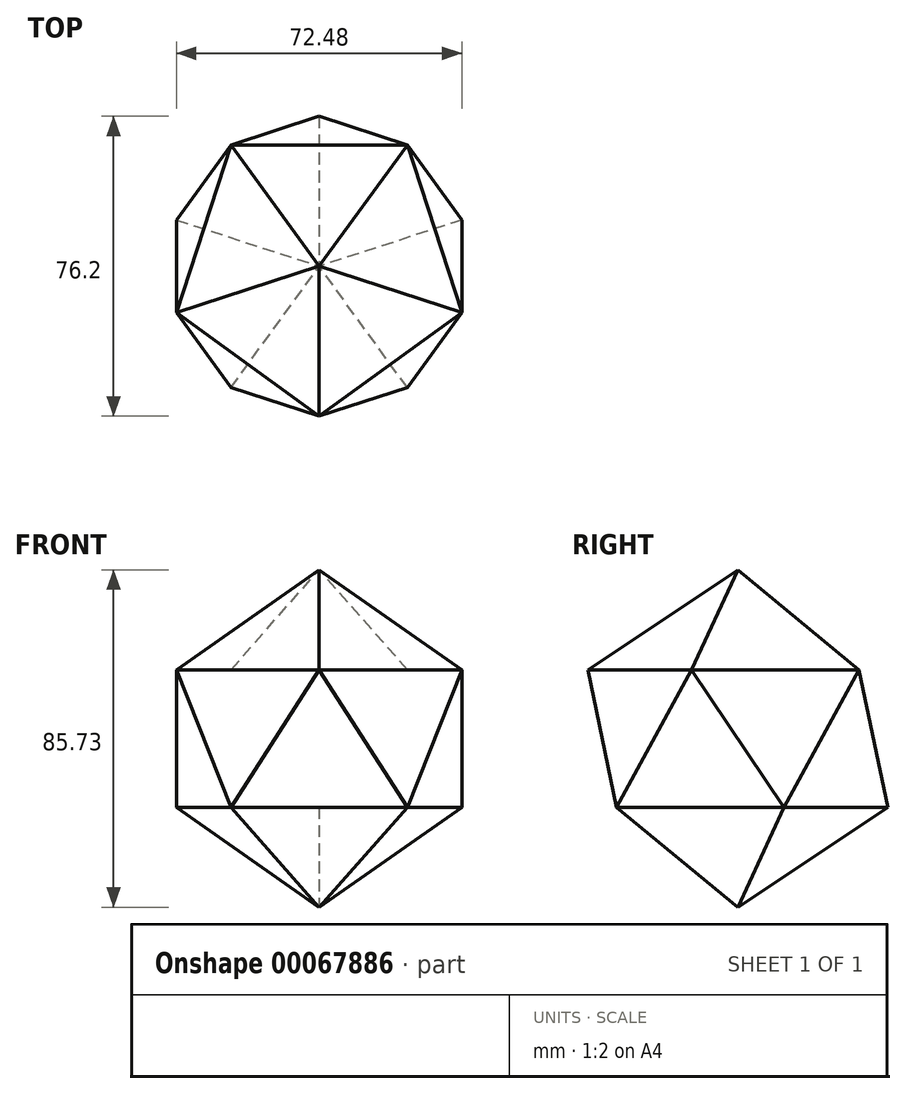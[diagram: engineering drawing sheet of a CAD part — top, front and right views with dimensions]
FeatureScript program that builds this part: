
annotation { "Feature Type Name" : "Feature", "Feature Type Description" : "" }
export const myFeature = defineFeature(function(context is Context, id is Id, definition is map)
    precondition{}
    {
        {
            var Q0;
            Q0=qCreatedBy(makeId("Top.planeOp"),FACE);
            var sketch = newSketch(context, id + "F0", { "sketchPlane" : qUnion([Q0])});
            skPoint(sketch, "E0", {"position": v(0, 0) * mm});
            skSolve(sketch);
        }
        {
            var Q0;
            Q0=qCreatedBy(makeId("Top.planeOp"),FACE);
            cPlane(context, id + "F1", {"entities" : qUnion([Q0]), "cplaneType" : CPlaneType.OFFSET, "offset" : 25.4 * mm, "width" : 152.4 * mm, "height" : 152.4 * mm});
        }
        {
            var Q0;
            Q0=qCreatedBy(id+"F1.planeOp",FACE);
            cPlane(context, id + "F2", {"entities" : qUnion([Q0]), "cplaneType" : CPlaneType.OFFSET, "offset" : 34.92 * mm, "width" : 152.4 * mm, "height" : 152.4 * mm});
        }
        {
            var Q0;
            Q0=qCreatedBy(id+"F2.planeOp",FACE);
            cPlane(context, id + "F3", {"entities" : qUnion([Q0]), "cplaneType" : CPlaneType.OFFSET, "offset" : 25.4 * mm, "width" : 152.4 * mm, "height" : 152.4 * mm});
        }
        {
            var Q0;
            Q0=qCreatedBy(id+"F1.planeOp",FACE);
            var sketch = newSketch(context, id + "F4", { "sketchPlane" : qUnion([Q0])});
            skCircle(sketch, "E1.cCircle", {"center": v(0, 0) * mm, "radius": 38.1 * mm, "construction": true});
            skLineSegment(sketch, "E1.0", {"start": v(-36.24, 11.77) * mm, "end": v(0, 38.1) * mm});
            skLineSegment(sketch, "E1.1", {"start": v(0, 38.1) * mm, "end": v(36.24, 11.77) * mm});
            skLineSegment(sketch, "E1.2", {"start": v(36.24, 11.77) * mm, "end": v(22.4, -30.82) * mm});
            skLineSegment(sketch, "E1.3", {"start": v(22.4, -30.82) * mm, "end": v(-22.4, -30.82) * mm});
            skLineSegment(sketch, "E1.4", {"start": v(-22.4, -30.82) * mm, "end": v(-36.24, 11.77) * mm});
            skSolve(sketch);
        }
        {
            var Q0;
            Q0=qCreatedBy(id+"F2.planeOp",FACE);
            var sketch = newSketch(context, id + "F5", { "sketchPlane" : qUnion([Q0])});
            skCircle(sketch, "E2.cCircle", {"center": v(0, 0) * mm, "radius": 38.1 * mm, "construction": true});
            skLineSegment(sketch, "E2.0", {"start": v(0, -38.1) * mm, "end": v(-36.24, -11.77) * mm});
            skLineSegment(sketch, "E2.1", {"start": v(-36.24, -11.77) * mm, "end": v(-22.4, 30.82) * mm});
            skLineSegment(sketch, "E2.2", {"start": v(-22.4, 30.82) * mm, "end": v(22.4, 30.82) * mm});
            skLineSegment(sketch, "E2.3", {"start": v(22.4, 30.82) * mm, "end": v(36.24, -11.77) * mm});
            skLineSegment(sketch, "E2.4", {"start": v(36.24, -11.77) * mm, "end": v(0, -38.1) * mm});
            skSolve(sketch);
        }
        {
            var Q0;
            Q0=qCreatedBy(id+"F3.planeOp",FACE);
            var sketch = newSketch(context, id + "F6", { "sketchPlane" : qUnion([Q0])});
            skPoint(sketch, "E3", {"position": v(0, 0) * mm});
            skSolve(sketch);
        }
        {
            var Q0;
            Q0=sQuery(id+"F4.wireOp",EDGE,"E1.3");
            var Q1;
            Q1=sQuery(id+"F5.wireOp",VERTEX,"E2.4.end");
            loft(context, id + "F7", {"bodyType" : ToolBodyType.SURFACE, "wireProfilesArray" : [{ "wireProfileEntities" : qUnion([Q0]) }, { "wireProfileEntities" : qUnion([Q1]) }]});
        }
        {
            var Q0;
            Q0=qCreatedBy(makeId("Right.planeOp"),FACE);
            var sketch = newSketch(context, id + "F8", { "sketchPlane" : qUnion([Q0])});
            skLineSegment(sketch, "E4", {"start": v(0, -22.28) * mm, "end": v(0, 85.26) * mm, "construction": true});
            skSolve(sketch);
        }
        {
            var Q0;
            Q0=makeQuery(id+"F7.opLoft","SWEPT_BODY",BODY,{"disambiguationData":[OSD([sQuery(id+"F4.wireOp",EDGE,"E1.3"),sQuery(id+"F5.wireOp",VERTEX,"E2.4.end")])]});
            var Q1;
            Q1=sQuery(id+"F8.wireOp",EDGE,"E4");
            circularPattern(context, id + "F9", {"entities" : qUnion([Q0]), "axis" : qUnion([Q1]), "angle" : 360 * degree, "instanceCount" : 5, "equalSpace" : true});
        }
        {
            var Q0;
            Q0=sQuery(id+"F4.wireOp",VERTEX,"E1.3.start");
            var Q1;
            Q1=makeQuery(id+"F5.imprint","IMPRINT",FACE,{"disambiguationData":[TD([[makeQuery(id+"F5.imprint","IMPRINT",EDGE,{"derivedFrom":sQuery(id+"F5.wireOp",EDGE,"E2.0")}),-1.0]])]});
            var Q2;
            Q2=sQuery(id+"F4.wireOp",VERTEX,"E1.4.start");
            var Q3;
            Q3=sQuery(id+"F5.wireOp",EDGE,"E2.0");
            loft(context, id + "F10", {"bodyType" : ToolBodyType.SURFACE, "sheetProfilesArray" : [{ "sheetProfileEntities" : qUnion([Q0]) }, { "sheetProfileEntities" : qUnion([Q1]) }], "wireProfilesArray" : [{ "wireProfileEntities" : qUnion([Q2]) }, { "wireProfileEntities" : qUnion([Q3]) }]});
        }
        {
            var Q0;
            Q0=qCreatedBy(makeId("Right.planeOp"),FACE);
            var sketch = newSketch(context, id + "F11", { "sketchPlane" : qUnion([Q0])});
            skLineSegment(sketch, "E5", {"start": v(0, -11.8) * mm, "end": v(0, 95.91) * mm, "construction": true});
            skSolve(sketch);
        }
        {
            var Q0;
            Q0=makeQuery(id+"F10.opLoft","SWEPT_BODY",BODY,{"disambiguationData":[OSD([sQuery(id+"F4.wireOp",VERTEX,"E1.4.start"),sQuery(id+"F5.wireOp",EDGE,"E2.0")])]});
            var Q1;
            Q1=sQuery(id+"F11.wireOp",EDGE,"E5");
            circularPattern(context, id + "F12", {"entities" : qUnion([Q0]), "axis" : qUnion([Q1]), "angle" : 360 * degree, "instanceCount" : 5, "equalSpace" : true});
        }
        {
            var Q0;
            Q0 = qSketchRegion(id + "F5", true);
            var Q1;
            Q1 = qSketchRegion(id + "F6", true);
            var Q2;
            Q2=sQuery(id+"F5.wireOp",EDGE,"E2.0");
            var Q3;
            Q3=sQuery(id+"F6.wireOp",VERTEX,"E3");
            loft(context, id + "F13", {"bodyType" : ToolBodyType.SURFACE, "sheetProfilesArray" : [{ "sheetProfileEntities" : qUnion([Q0]) }, { "sheetProfileEntities" : qUnion([Q1]) }], "wireProfilesArray" : [{ "wireProfileEntities" : qUnion([Q2]) }, { "wireProfileEntities" : qUnion([Q3]) }]});
        }
        {
            var Q0;
            Q0=qCreatedBy(makeId("Right.planeOp"),FACE);
            var sketch = newSketch(context, id + "F14", { "sketchPlane" : qUnion([Q0])});
            skLineSegment(sketch, "E6", {"start": v(0, -23.63) * mm, "end": v(0, 91.22) * mm, "construction": true});
            skSolve(sketch);
        }
        {
            var Q0;
            Q0=makeQuery(id+"F13.opLoft","SWEPT_BODY",BODY,{"disambiguationData":[OSD([sQuery(id+"F5.wireOp",EDGE,"E2.0"),sQuery(id+"F6.wireOp",VERTEX,"E3")])]});
            var Q1;
            Q1=sQuery(id+"F14.wireOp",EDGE,"E6");
            circularPattern(context, id + "F15", {"entities" : qUnion([Q0]), "axis" : qUnion([Q1]), "angle" : 360 * degree, "instanceCount" : 5, "equalSpace" : true});
        }
        {
            var Q0;
            Q0=makeQuery(id+"F9.opPattern","COPY",EDGE,{"derivedFrom":makeQuery(id+"F7.opLoft","MID_CAP_EDGE",EDGE,{"disambiguationData":[OSD([sQuery(id+"F4.wireOp",VERTEX,"E1.3.start"),sQuery(id+"F4.wireOp",VERTEX,"E1.3.end"),sQuery(id+"F4.wireOp",EDGE,"E1.3")])],"capPos":0.0}),"instanceName":"4"});
            var Q1;
            Q1=sQuery(id+"F0.wireOp",VERTEX,"E0");
            loft(context, id + "F16", {"bodyType" : ToolBodyType.SURFACE, "wireProfilesArray" : [{ "wireProfileEntities" : qUnion([Q0]) }, { "wireProfileEntities" : qUnion([Q1]) }]});
        }
        {
            var Q0;
            Q0=qCreatedBy(makeId("Right.planeOp"),FACE);
            var sketch = newSketch(context, id + "F17", { "sketchPlane" : qUnion([Q0])});
            skLineSegment(sketch, "E7", {"start": v(0, -20.25) * mm, "end": v(0, 87.86) * mm, "construction": true});
            skSolve(sketch);
        }
        {
            var Q0;
            Q0=makeQuery(id+"F16.opLoft","SWEPT_BODY",BODY,{"disambiguationData":[OSD([sQuery(id+"F0.wireOp",VERTEX,"E0"),sQuery(id+"F4.wireOp",VERTEX,"E1.3.start"),sQuery(id+"F4.wireOp",VERTEX,"E1.3.end"),sQuery(id+"F4.wireOp",EDGE,"E1.3")])]});
            var Q1;
            Q1=sQuery(id+"F17.wireOp",EDGE,"E7");
            circularPattern(context, id + "F18", {"entities" : qUnion([Q0]), "axis" : qUnion([Q1]), "angle" : 360 * degree, "instanceCount" : 5, "equalSpace" : true});
        }
    });
